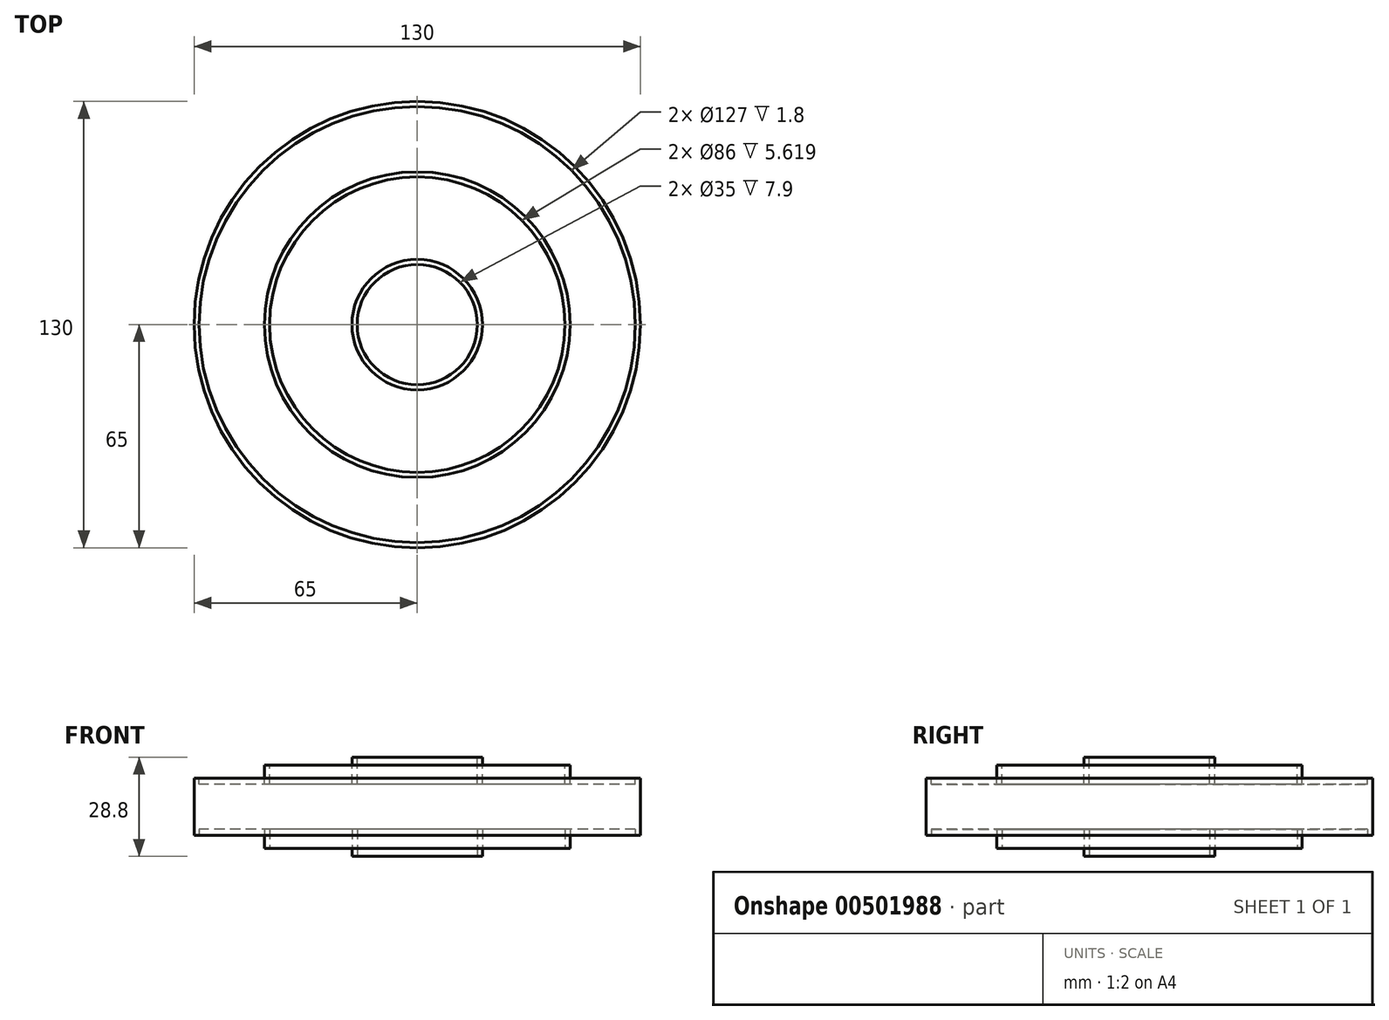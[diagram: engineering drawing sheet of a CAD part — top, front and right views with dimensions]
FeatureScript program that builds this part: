
annotation { "Feature Type Name" : "Feature", "Feature Type Description" : "" }
export const myFeature = defineFeature(function(context is Context, id is Id, definition is map)
    precondition{}
    {
        {
            var Q0;
            Q0=qCreatedBy(makeId("Front.planeOp"),FACE);
            var sketch = newSketch(context, id + "F0", { "sketchPlane" : qUnion([Q0])});
            skLineSegment(sketch, "E0", {"start": v(0, 0) * mm, "end": v(65, 0) * mm});
            skLineSegment(sketch, "E1", {"start": v(65, 0) * mm, "end": v(65, 8.3) * mm});
            skLineSegment(sketch, "E2", {"start": v(65, 8.3) * mm, "end": v(63.5, 8.3) * mm});
            skLineSegment(sketch, "E3", {"start": v(63.5, 8.3) * mm, "end": v(63.5, 6.5) * mm});
            skLineSegment(sketch, "E4", {"start": v(63.5, 6.5) * mm, "end": v(44.5, 6.5) * mm});
            skLineSegment(sketch, "E5", {"start": v(44.5, 6.5) * mm, "end": v(44.5, 12.1) * mm});
            skLineSegment(sketch, "E6", {"start": v(44.5, 12.1) * mm, "end": v(43, 12.1) * mm});
            skLineSegment(sketch, "E7", {"start": v(43, 12.1) * mm, "end": v(43, 6.48) * mm});
            skLineSegment(sketch, "E8", {"start": v(43, 6.48) * mm, "end": v(19, 6.48) * mm});
            skLineSegment(sketch, "E9", {"start": v(17.5, 6.5) * mm, "end": v(0, 6.5) * mm});
            skLineSegment(sketch, "E10", {"start": v(0, 6.5) * mm, "end": v(0, 0) * mm});
            skLineSegment(sketch, "E11", {"start": v(17.5, 6.5) * mm, "end": v(17.5, 14.4) * mm});
            skLineSegment(sketch, "E12", {"start": v(19, 6.48) * mm, "end": v(19, 14.38) * mm});
            skLineSegment(sketch, "E13", {"start": v(17.5, 14.4) * mm, "end": v(19, 14.38) * mm});
            skSolve(sketch);
        }
        {
            var Q0;
            Q0=makeQuery(id+"F0.imprint","IMPRINT",FACE,{"disambiguationData":[TD([[makeQuery(id+"F0.imprint","IMPRINT",EDGE,{"derivedFrom":sQuery(id+"F0.wireOp",EDGE,"E0")}),1.0]])]});
            var Q1;
            Q1=sQuery(id+"F0.wireOp",EDGE,"E10");
            revolve(context, id + "F1", {"entities" : qUnion([Q0]), "axis" : qUnion([Q1]), "revolveType" : RevolveType.FULL});
        }
        {
            var Q0;
            Q0=makeQuery(id+"F1.opRevolve","SWEPT_BODY",BODY,{"disambiguationData":[OSD([sQuery(id+"F0.wireOp",EDGE,"E0"),sQuery(id+"F0.wireOp",EDGE,"E1"),sQuery(id+"F0.wireOp",EDGE,"E2"),sQuery(id+"F0.wireOp",EDGE,"E3"),sQuery(id+"F0.wireOp",EDGE,"E4"),sQuery(id+"F0.wireOp",EDGE,"E5"),sQuery(id+"F0.wireOp",EDGE,"E6"),sQuery(id+"F0.wireOp",EDGE,"E7"),sQuery(id+"F0.wireOp",EDGE,"E8"),sQuery(id+"F0.wireOp",EDGE,"5YPTCmyY-6YKU-LiL6-u8zq-XvXLS9jic6AO"),sQuery(id+"F0.wireOp",EDGE,"fQRwUbhX-tsjL-CvtL-fsw9-C4C0SLajUJrB"),sQuery(id+"F0.wireOp",EDGE,"5Oe88dvq-rLBt-Kjcf-D9FV-EXcgm2x8rpkm"),sQuery(id+"F0.wireOp",EDGE,"E9"),sQuery(id+"F0.wireOp",EDGE,"E10")])]});
            var Q1;
            Q1=qCreatedBy(makeId("Top.planeOp"),FACE);
            mirror(context, id + "F2", {"operationType" : NewBodyOperationType.ADD, "entities" : qUnion([Q0]), "mirrorPlane" : qUnion([Q1])});
        }
    });
